# Revit family: VFB_VFB Plus 216-255mm
name_source: partatom
category: Specialty Equipment
revit_build: Autodesk Revit 2015 (Build: 20160512_0715(x64)
units: mm (PartAtom-declared; Revit-internal decimal feet)

## types (40) — shared parameters
Depth = 75 mm
Description = Firefly 102 Ventilated Fire Barrier
IFC Classification = Building Element Proxy
Length = 1000 mm
Manufacturer = Tenmat ltd
Material/Grade = Firefly 102
Performance = BS EN 1366-3:2009 & BS 476, ETA-12/0332, 1224-CPR-0341, CE Marked
URL = https://www.tenmat.com
Youtube Clip = https://www.youtube.com

## per-type parameters (varying)
| type | Seal Type | Tenmat Item Number | Width |
| VFB Plus 216.0 x 75.0 x 1000mm | VFB Plus 260 | I102MP21600075100000 | 216 mm  [stored 0.708661 ft] |
| VFB Plus 217.0 x 75.0 x 1000mm | VFB Plus 261 | I102MP21700075100000 | 217 mm  [stored 0.711942 ft] |
| VFB Plus 218.0 x 75.0 x 1000mm | VFB Plus 262 | I102MP21800075100000 | 218 mm  [stored 0.715223 ft] |
| VFB Plus 219.0 x 75.0 x 1000mm | VFB Plus 263 | I102MP21900075100000 | 219 mm  [stored 0.718504 ft] |
| VFB Plus 220.0 x 75.0 x 1000mm | VFB Plus 264 | I102MP22000075100000 | 220 mm  [stored 0.721785 ft] |
| VFB Plus 221.0 x 75.0 x 1000mm | VFB Plus 265 | I102MP22100075100000 | 221 mm  [stored 0.725066 ft] |
| VFB Plus 222.0 x 75.0 x 1000mm | VFB Plus 266 | I102MP22200075100000 | 222 mm |
| VFB Plus 223.0 x 75.0 x 1000mm | VFB Plus 267 | I102MP22300075100000 | 223 mm  [stored 0.731627 ft] |
| VFB Plus 224.0 x 75.0 x 1000mm | VFB Plus 268 | I102MP22400075100000 | 224 mm  [stored 0.734908 ft] |
| VFB Plus 225.0 x 75.0 x 1000mm | VFB Plus 269 | I102MP22500075100000 | 225 mm  [stored 0.738189 ft] |
| VFB Plus 226.0 x 75.0 x 1000mm | VFB Plus 270 | I102MP22600075100000 | 226 mm  [stored 0.74147 ft] |
| VFB Plus 227.0 x 75.0 x 1000mm | VFB Plus 271 | I102MP22700075100000 | 227 mm  [stored 0.744751 ft] |
| VFB Plus 228.0 x 75.0 x 1000mm | VFB Plus 272 | I102MP22800075100000 | 228 mm  [stored 0.748031 ft] |
| VFB Plus 229.0 x 75.0 x 1000mm | VFB Plus 273 | I102MP22900075100000 | 229 mm |
| VFB Plus 230.0 x 75.0 x 1000mm | VFB Plus 274 | I102MP23000075100000 | 230 mm  [stored 0.754593 ft] |
| VFB Plus 231.0 x 75.0 x 1000mm | VFB Plus 275 | I102MP23100075100000 | 231 mm  [stored 0.757874 ft] |
| VFB Plus 232.0 x 75.0 x 1000mm | VFB Plus 276 | I102MP07500075100000
I102MP23200075100000 | 232 mm  [stored 0.761155 ft] |
| VFB Plus 233.0 x 75.0 x 1000mm | VFB Plus 277 | I102MP23300075100000 | 233 mm  [stored 0.764436 ft] |
| VFB Plus 234.0 x 75.0 x 1000mm | VFB Plus 278 | I102MP23400075100000 | 234 mm  [stored 0.767717 ft] |
| VFB Plus 235.0 x 75.0 x 1000mm | VFB Plus 279 | I102MP23500075100000 | 235 mm  [stored 0.770997 ft] |
| VFB Plus 236.0 x 75.0 x 1000mm | VFB Plus 280 | I102MP23600075100000 | 236 mm |
| VFB Plus 237.0 x 75.0 x 1000mm | VFB Plus 281 | I102MP23700075100000 | 237 mm  [stored 0.777559 ft] |
| VFB Plus 238.0 x 75.0 x 1000mm | VFB Plus 282 | I102MP23800075100000
I102MP01600075100000 | 238 mm  [stored 0.78084 ft] |
| VFB Plus 239.0 x 75.0 x 1000mm | VFB Plus 283 | I102MP23900075100000 | 239 mm  [stored 0.784121 ft] |
| VFB Plus 240.0 x 75.0 x 1000mm | VFB Plus 284 | I102MP24000075100000 | 240 mm  [stored 0.787402 ft] |
| VFB Plus 241.0 x 75.0 x 1000mm | VFB Plus 285 | I102MP24100075100000 | 241 mm  [stored 0.790682 ft] |
| VFB Plus 242.0 x 75.0 x 1000mm | VFB Plus 286 | I102MP24200075100000 | 242 mm  [stored 0.793963 ft] |
| VFB Plus 243.0 x 75.0 x 1000mm | VFB Plus 287 | I102MP24300075100000 | 243 mm |
| VFB Plus 244.0 x 75.0 x 1000mm | VFB Plus 288 | I102MP24400075100000 | 244 mm  [stored 0.800525 ft] |
| VFB Plus 245.0 x 75.0 x 1000mm | VFB Plus 289 | I102MP24500075100000 | 245 mm  [stored 0.803806 ft] |
| VFB Plus 246.0 x 75.0 x 1000mm | VFB Plus 290 | I102MP24600075100000 | 246 mm  [stored 0.807087 ft] |
| VFB Plus 247.0 x 75.0 x 1000mm | VFB Plus 291 | I102MP24000075100000
I102MP24700075100000 | 247 mm |
| VFB Plus 248.0 x 75.0 x 1000mm | VFB Plus 292 | I102MP24800075100000 | 248 mm  [stored 0.813648 ft] |
| VFB Plus 249.0 x 75.0 x 1000mm | VFB Plus 293 | I102MP24900075100000 | 249 mm  [stored 0.816929 ft] |
| VFB Plus 250.0 x 75.0 x 1000mm | VFB Plus 294 | I102MP25000075100000 | 250 mm  [stored 0.82021 ft] |
| VFB Plus 251.0 x 75.0 x 1000mm | VFB Plus 295 | I102MP25100075100000 | 251 mm  [stored 0.823491 ft] |
| VFB Plus 252.0 x 75.0 x 1000mm | VFB Plus 296 | I102MP25200075100000
I102MP01600075100000 | 252 mm  [stored 0.826772 ft] |
| VFB Plus 253.0 x 75.0 x 1000mm | VFB Plus 297 | I102MP25300075100000 | 253 mm  [stored 0.830052 ft] |
| VFB Plus 254.0 x 75.0 x 1000mm | VFB Plus 298 | I102MP25400075100000 | 254 mm |
| VFB Plus 255.0 x 75.0 x 1000mm | VFB Plus 299 | I102MP25500075100000 | 255 mm |

note: [stored X ft] marks values corroborated as IEEE doubles in the binary element streams (Revit-internal decimal feet)

## geometry (parser evidence)
native form markers: Blend x2, Sweep x9
no freeform markers — native parametric forms only
